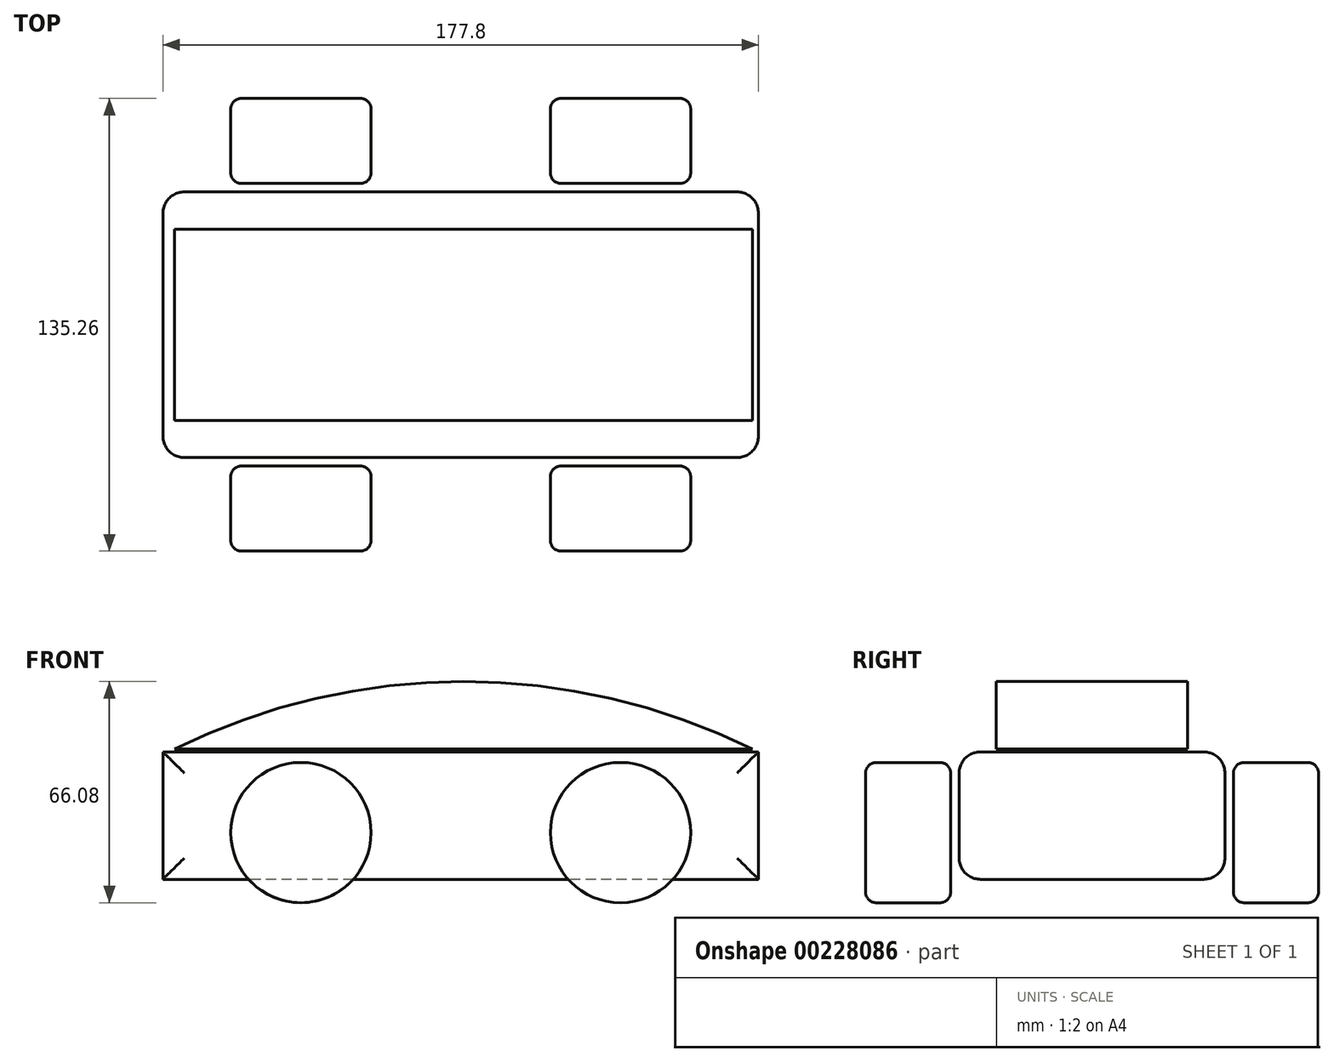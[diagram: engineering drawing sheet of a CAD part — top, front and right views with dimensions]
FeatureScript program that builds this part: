
annotation { "Feature Type Name" : "Feature", "Feature Type Description" : "" }
export const myFeature = defineFeature(function(context is Context, id is Id, definition is map)
    precondition{}
    {
        {
            var Q0;
            Q0=qCreatedBy(makeId("Front.planeOp"),FACE);
            var sketch = newSketch(context, id + "F0", { "sketchPlane" : qUnion([Q0])});
            skPoint(sketch, "E0.middle", {"position": v(0, 0) * mm});
            skLineSegment(sketch, "E1", {"start": v(-73.6, -26.03) * mm, "end": v(102.5, -26.03) * mm, "construction": true});
            skLineSegment(sketch, "E2", {"start": v(59.19, -26.03) * mm, "end": v(59.19, -19.05) * mm});
            skLineSegment(sketch, "E3.bottom", {"start": v(88.9, -19.05) * mm, "end": v(-88.9, -19.05) * mm});
            skLineSegment(sketch, "E3.top", {"start": v(88.9, 19.05) * mm, "end": v(-88.9, 19.05) * mm});
            skLineSegment(sketch, "E3.left", {"start": v(88.9, -19.05) * mm, "end": v(88.9, 19.05) * mm});
            skLineSegment(sketch, "E3.right", {"start": v(-88.9, -19.05) * mm, "end": v(-88.9, 19.05) * mm});
            skSolve(sketch);
        }
        {
            var Q0;
            Q0=qCreatedBy(makeId("Front.planeOp"),FACE);
            var sketch = newSketch(context, id + "F1", { "sketchPlane" : qUnion([Q0])});
            skCircle(sketch, "E4", {"center": v(47.72, -5.08) * mm, "radius": 20.96 * mm});
            skSolve(sketch);
        }
        {
            var Q0;
            Q0=makeQuery(id+"F0.imprint","IMPRINT",FACE,{"disambiguationData":[TD([[makeQuery(id+"F0.imprint","IMPRINT",EDGE,{"derivedFrom":sQuery(id+"F0.wireOp",EDGE,"E3.top")}),1.0]])]});
            extrude(context, id + "F2", {"entities" : qUnion([Q0]), "endBound" : BoundingType.SYMMETRIC, "depth" : 79.38 * mm});
        }
        {
            var Q0;
            Q0=makeQuery(id+"F2.opExtrude","CAP_FACE",FACE,{"disambiguationData":[OSD([sQuery(id+"F0.wireOp",EDGE,"E3.bottom"),sQuery(id+"F0.wireOp",EDGE,"E3.top"),sQuery(id+"F0.wireOp",EDGE,"E3.left"),sQuery(id+"F0.wireOp",EDGE,"E3.right")])],"isStart":false});
            cPlane(context, id + "F3", {"entities" : qUnion([Q0]), "cplaneType" : CPlaneType.OFFSET, "offset" : 2.54 * mm, "width" : 152.4 * mm, "height" : 152.4 * mm});
        }
        {
            var Q0;
            Q0=qCreatedBy(id+"F3.planeOp",FACE);
            var sketch = newSketch(context, id + "F4", { "sketchPlane" : qUnion([Q0])});
            skCircle(sketch, "E5.0", {"center": v(47.72, -5.08) * mm, "radius": 20.96 * mm});
            skSolve(sketch);
        }
        {
            var Q0;
            Q0=makeQuery(id+"F4.imprint","IMPRINT",FACE,{"disambiguationData":[TD([[makeQuery(id+"F4.imprint","IMPRINT",EDGE,{"derivedFrom":sQuery(id+"F4.wireOp",EDGE,"E5.0")}),1.0]])]});
            var Q1;
            Q1=sQuery(id+"F4.wireOp",EDGE,"E5.0");
            extrude(context, id + "F5", {"entities" : qUnion([Q0]), "surfaceEntities" : qUnion([Q1]), "depth" : 25.4 * mm});
        }
        {
            var Q0;
            Q0=makeQuery(id+"F2.opExtrude","CAP_EDGE",EDGE,{"disambiguationData":[OSD([sQuery(id+"F0.wireOp",EDGE,"E3.top")])],"isStart":false});
            var Q1;
            Q1=makeQuery(id+"F2.opExtrude","CAP_EDGE",EDGE,{"disambiguationData":[OSD([sQuery(id+"F0.wireOp",EDGE,"E3.bottom")])],"isStart":false});
            var Q2;
            Q2=makeQuery(id+"F2.opExtrude","CAP_EDGE",EDGE,{"disambiguationData":[OSD([sQuery(id+"F0.wireOp",EDGE,"E3.right")])],"isStart":false});
            var Q3;
            Q3=makeQuery(id+"F2.opExtrude","CAP_EDGE",EDGE,{"disambiguationData":[OSD([sQuery(id+"F0.wireOp",EDGE,"E3.left")])],"isStart":false});
            var Q4;
            Q4=makeQuery(id+"F2.opExtrude","CAP_EDGE",EDGE,{"disambiguationData":[OSD([sQuery(id+"F0.wireOp",EDGE,"E3.left")])],"isStart":true});
            var Q5;
            Q5=makeQuery(id+"F2.opExtrude","CAP_EDGE",EDGE,{"disambiguationData":[OSD([sQuery(id+"F0.wireOp",EDGE,"E3.top")])],"isStart":true});
            var Q6;
            Q6=makeQuery(id+"F2.opExtrude","CAP_EDGE",EDGE,{"disambiguationData":[OSD([sQuery(id+"F0.wireOp",EDGE,"E3.right")])],"isStart":true});
            var Q7;
            Q7=makeQuery(id+"F2.opExtrude","CAP_EDGE",EDGE,{"disambiguationData":[OSD([sQuery(id+"F0.wireOp",EDGE,"E3.bottom")])],"isStart":true});
            fillet(context, id + "F6", {"entities" : qUnion([Q0, Q1, Q2, Q3, Q4, Q5, Q6, Q7]), "radius" : 6.35 * mm, "tangentPropagation" : true, "allowEdgeOverflow" : false});
        }
        {
            var Q0;
            Q0=makeQuery(id+"F5.opExtrude","CAP_EDGE",EDGE,{"disambiguationData":[OSD([sQuery(id+"F4.wireOp",EDGE,"E5.0")])],"isStart":false});
            var Q1;
            Q1=makeQuery(id+"F5.opExtrude","CAP_EDGE",EDGE,{"disambiguationData":[OSD([sQuery(id+"F4.wireOp",EDGE,"E5.0")])],"isStart":true});
            fillet(context, id + "F7", {"entities" : qUnion([Q0, Q1]), "radius" : 3.17 * mm, "tangentPropagation" : true, "allowEdgeOverflow" : false});
        }
        {
            var Q0;
            Q0=makeQuery(id+"F5.opExtrude","SWEPT_BODY",BODY,{"disambiguationData":[OSD([sQuery(id+"F4.wireOp",EDGE,"E5.0")])]});
            var Q1;
            Q1=qCreatedBy(makeId("Front.planeOp"),FACE);
            mirror(context, id + "F8", {"entities" : qUnion([Q0]), "mirrorPlane" : qUnion([Q1])});
        }
        {
            var Q0;
            Q0=makeQuery(id+"F5.opExtrude","SWEPT_BODY",BODY,{"disambiguationData":[OSD([sQuery(id+"F4.wireOp",EDGE,"E5.0")])]});
            var Q1;
            Q1=makeQuery(id+"F8.opPattern","COPY",BODY,{"derivedFrom":makeQuery(id+"F5.opExtrude","SWEPT_BODY",BODY,{"disambiguationData":[OSD([sQuery(id+"F4.wireOp",EDGE,"E5.0")])]}),"instanceName":"1"});
            var Q2;
            Q2=qCreatedBy(makeId("Right.planeOp"),FACE);
            mirror(context, id + "F9", {"entities" : qUnion([Q0, Q1]), "mirrorPlane" : qUnion([Q2])});
        }
        {
            var Q0;
            Q0=qCreatedBy(makeId("Front.planeOp"),FACE);
            var sketch = newSketch(context, id + "F10", { "sketchPlane" : qUnion([Q0])});
            skLineSegment(sketch, "E6", {"start": v(-85.5, 19.87) * mm, "end": v(92.3, 19.87) * mm});
            skLineSegment(sketch, "E7", {"start": v(-85.5, 19.87) * mm, "end": v(-46.8, 39) * mm});
            skArc(sketch, "E8", {"start": v(87.14, 19.87) * mm, "mid": v(0.82, 40.04) * mm, "end": v(-85.5, 19.87) * mm});
            skSolve(sketch);
        }
        {
            var Q0;
            {var subQ0=sQuery(id+"F10.wireOp",EDGE,"E8");Q0=makeQuery(id+"F10.imprint","IMPRINT",FACE,{"disambiguationData":[TD([[makeQuery(id+"F10.imprint","IMPRINT",EDGE,{"derivedFrom":subQ0}),1.0]])]});}
            var Q1;
            Q1=sQuery(id+"F10.wireOp",EDGE,"E8");
            var Q2;
            Q2=sQuery(id+"F10.wireOp",EDGE,"E6");
            extrude(context, id + "F11", {"entities" : qUnion([Q0]), "surfaceEntities" : qUnion([Q1, Q2]), "endBound" : BoundingType.SYMMETRIC, "depth" : 57.15 * mm});
        }
    });
